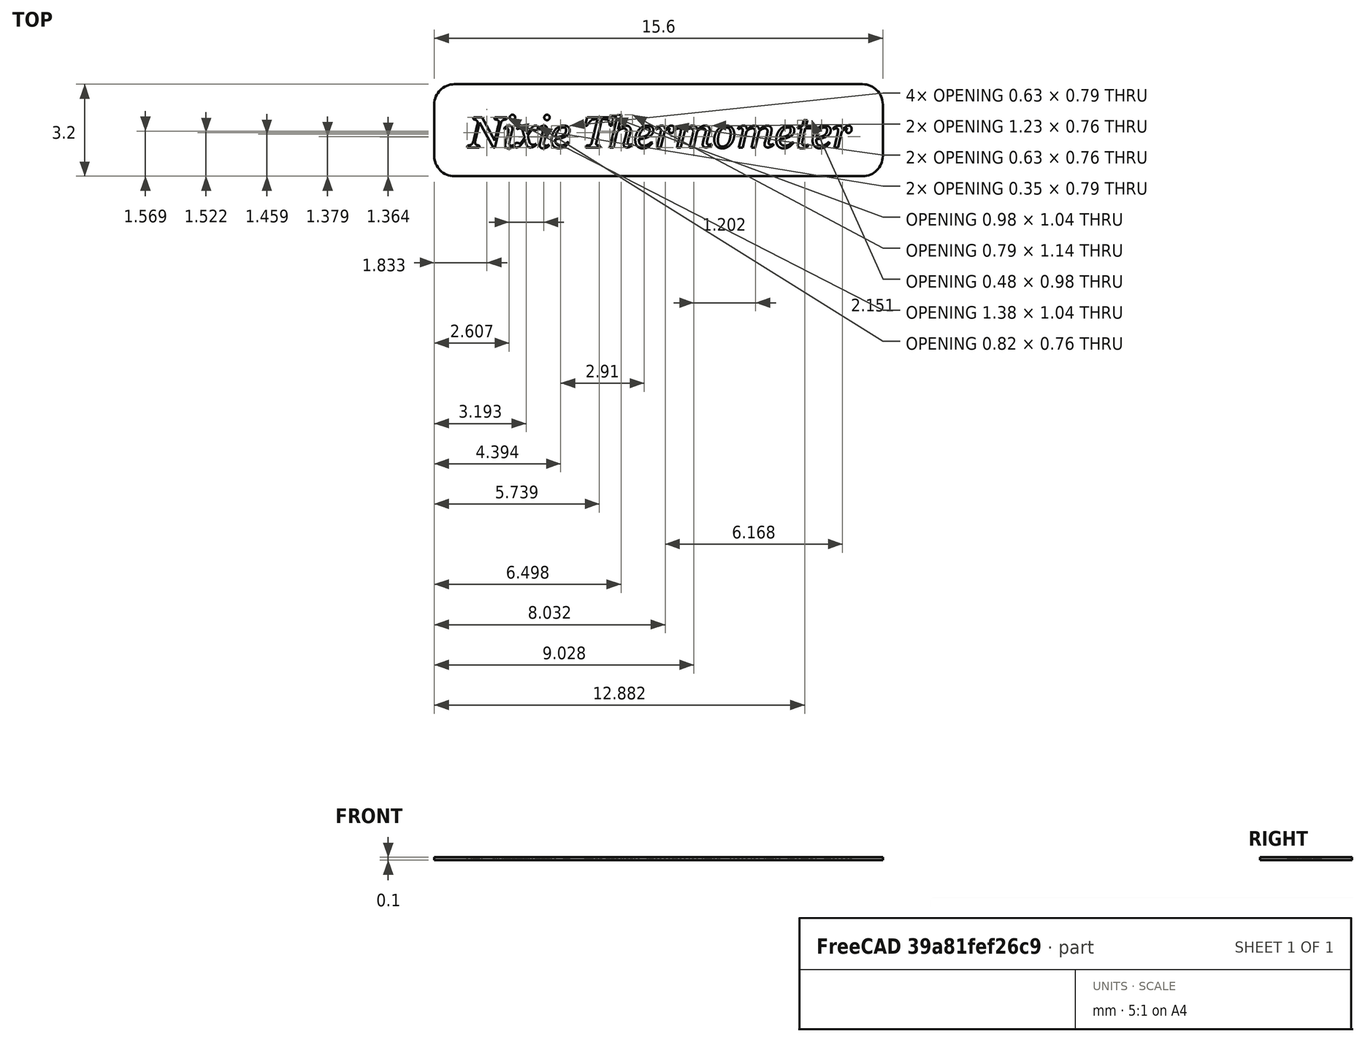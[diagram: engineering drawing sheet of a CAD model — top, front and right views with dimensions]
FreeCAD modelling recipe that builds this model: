
FCSTD DOCUMENT  (FreeCAD 0.16R6712 (Git))
Label: tag3
License: All rights reserved
LicenseURL: http://en.wikipedia.org/wiki/All_rights_reserved
objects: Part::Extrusion×2, Part::Part2DObjectPython×1, Sketcher::SketchObject×1, Part::Cut×1, Mesh::Feature×1
note: 5 computed .brp shape members not serialized (recipe doc carries the construction recipe); baked Part::Feature solids carry a one-line shape summary decoded from their .brp

FEATURE [Part::Part2DObjectPython] ShapeString  # Draft 2D object (typed FeaturePython)
  FontFile = <path>
  Placement = pos=(0,0.4,0) rot=(0,0,1;0rad)
  Size = 1.15
  String = Nixie Thermometer
  Tracking = 0
FEATURE [Part::Extrusion] Extrude
  Base = -> ShapeString
  Dir = (0,0,0.4)
  Placement = pos=(0,0,-0.2) rot=(0,0,1;0rad)
  Solid = true
FEATURE [Sketcher::SketchObject] Sketch
  sketch-geometry (8):
    g0: LineSegment StartX=-0.5 StartY=2.6 StartZ=0 EndX=13.7 EndY=2.6 EndZ=0
    g1: LineSegment StartX=14.4 StartY=1.9 StartZ=0 EndX=14.4 EndY=0.1 EndZ=0
    g2: LineSegment StartX=13.7 StartY=-0.6 StartZ=0 EndX=-0.5 EndY=-0.6 EndZ=0
    g3: LineSegment StartX=-1.2 StartY=0.1 StartZ=0 EndX=-1.2 EndY=1.9 EndZ=0
    g4: ArcOfCircle CenterX=-0.5 CenterY=1.9 CenterZ=0 NormalX=0 NormalY=0 NormalZ=1 Radius=0.7 StartAngle=1.5708 EndAngle=3.14159
    g5: ArcOfCircle CenterX=-0.5 CenterY=0.1 CenterZ=0 NormalX=0 NormalY=0 NormalZ=1 Radius=0.7 StartAngle=3.14159 EndAngle=4.71239
    g6: ArcOfCircle CenterX=13.7 CenterY=0.1 CenterZ=0 NormalX=0 NormalY=0 NormalZ=1 Radius=0.7 StartAngle=4.71239 EndAngle=6.28319
    g7: ArcOfCircle CenterX=13.7 CenterY=1.9 CenterZ=0 NormalX=0 NormalY=0 NormalZ=1 Radius=0.7 StartAngle=0 EndAngle=1.5708
  constraints (20):
    c: Horizontal(g0)
    c: Horizontal(g2)
    c: Vertical(g1)
    c: Vertical(g3)
    c: Tangent(g0,g4) = 1.5708
    c: Tangent(g3,g4) = 1.5708
    c: Tangent(g3,g5) = 1.5708
    c: Tangent(g2,g5) = 1.5708
    c: Tangent(g2,g6) = 1.5708
    c: Tangent(g1,g6) = 1.5708
    c: Tangent(g1,g7) = 1.5708
    c: Tangent(g0,g7) = 1.5708
    c: Radius(g7) = 0.7
    c: Equal(g7,g4)
    c: Equal(g4,g5)
    c: Equal(g5,g6)
    c: DistanceY(g-1,g2) = -0.6
    c: DistanceX(g-2,g3) = -1.2
    c: Distance(g3,g1) = 15.6
    c: Distance(g2,g0) = 3.2
FEATURE [Part::Extrusion] Extrude001
  Base = -> Sketch
  Dir = (0,0,0.1)
  Solid = true
FEATURE [Part::Cut] Cut
  Base = -> Extrude001
  Tool = -> Extrude
FEATURE [Mesh::Feature] Mesh  label="Cut (Meshed)"
  Placement = pos=(-6.6,-9,7.3) rot=(0,0,1;0rad)
note: 1 file-system path scrubbed to <path> (originals preserved in the JSON sidecar)
